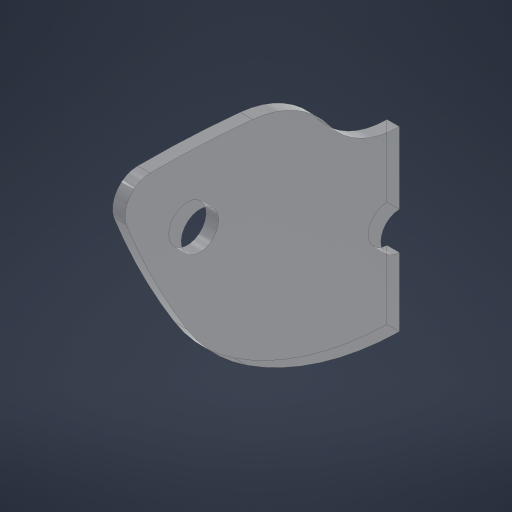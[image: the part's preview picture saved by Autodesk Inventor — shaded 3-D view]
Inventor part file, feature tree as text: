
AUTODESK INVENTOR PART (.ipt)
format: ipt  version: 2024 (Build 280153000, 153)  size: 216,576 bytes
history: native  units: in
note: dims shown in document units (in); Inventor stores cm internally (conversion verified against a paired STEP export)
features: sketch x1, extrude x1, hole x1
ambient origin geometry x8: Origin, YZ Plane, XZ Plane, XY Plane, X Axis, Y Axis, Z Axis, Center Point
bodies: Solid1 (feature_tree)
feature tree (3):
  sketch  "Sketch1"  dims[d0=0.5in d1=0.125in d2=1.0in d3=0.75in d4=1.0in d5=1.0in d6=0.5in d7=0.5in d8=1.25in d9=1.0in d10=1.0in d11=0.25in d12=0.25in d14=0.0in d15=0.0625in d16=0.75in d17=0.8108in d18=0.5635in d19=0.25in d20=0.375in d21=1.0in d22=0.1875in]
  extrude  "Extrusion1"  [1 undecoded]
  hole  "Hole1"  [1 undecoded]
note: 2 required parameter values undecoded (feature->parameter linkage not recoverable at this tier; creation-order binding heuristic only, values carry confidence <= 0.55)
